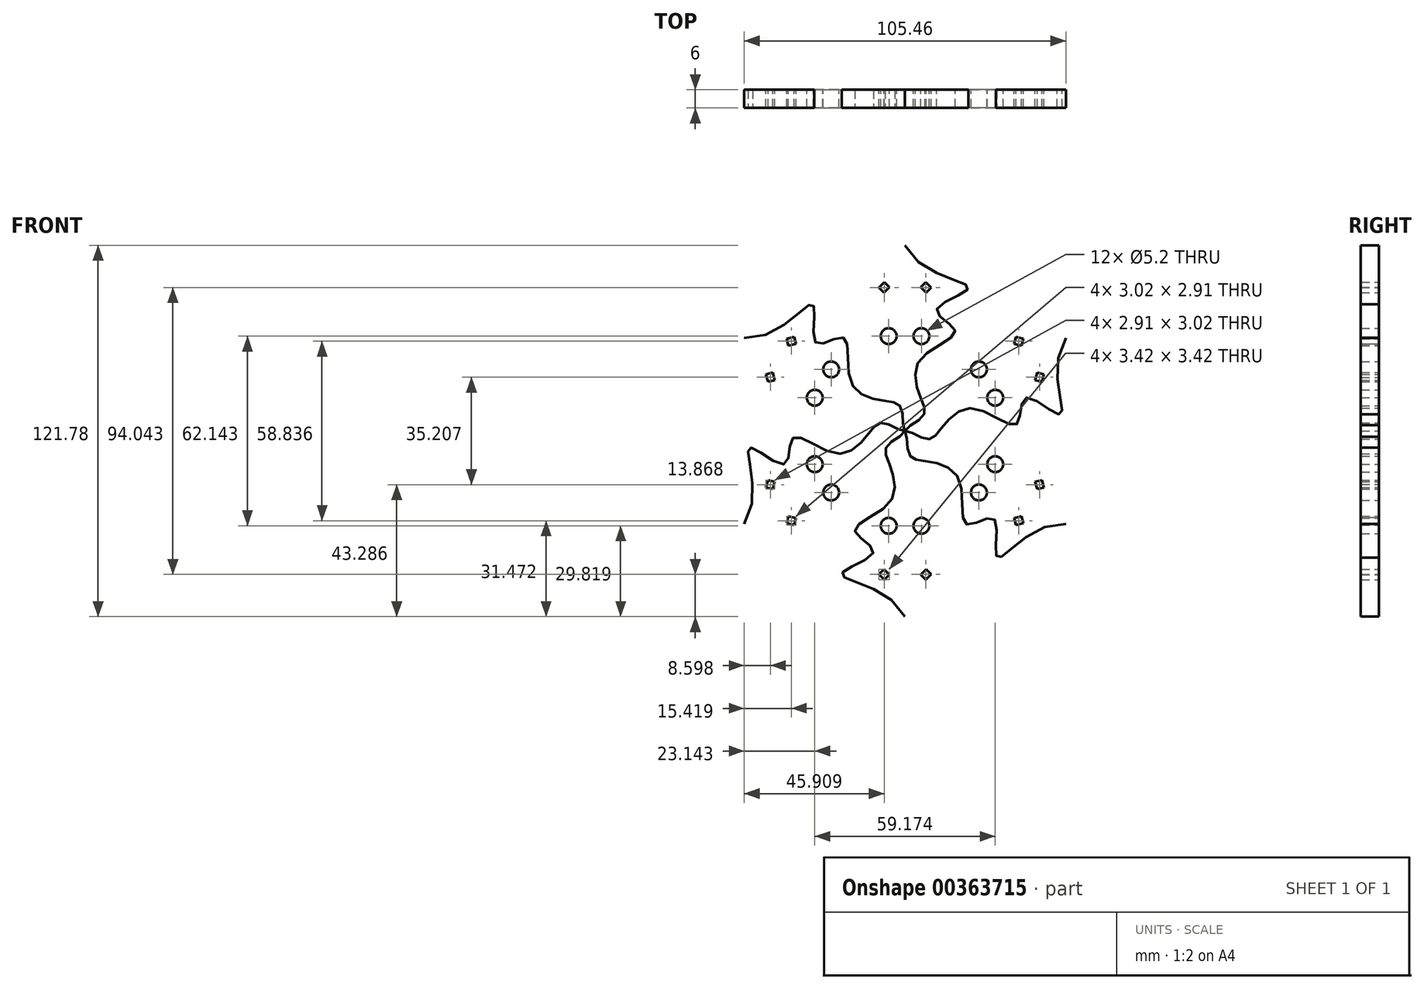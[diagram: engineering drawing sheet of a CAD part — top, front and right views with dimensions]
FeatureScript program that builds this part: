
annotation { "Feature Type Name" : "Feature", "Feature Type Description" : "" }
export const myFeature = defineFeature(function(context is Context, id is Id, definition is map)
    precondition{}
    {
        {
            var Q0;
            Q0=qCreatedBy(makeId("Front.planeOp"),FACE);
            var sketch = newSketch(context, id + "F0", { "sketchPlane" : qUnion([Q0])});
            skLineSegment(sketch, "E0", {"start": v(0, 0) * mm, "end": v(0, 65.18) * mm, "construction": true});
            skFitSpline(sketch, "E1", {"points": [v(0, 60.9) * mm, v(20.71, 46.79) * mm, v(10.36, 39.64) * mm, v(16.43, 32.86) * mm, v(4.83, 23.22) * mm, v(5.36, 10.36) * mm, v(5.9, 4.82) * mm, v(0, 0) * mm], "startDerivative": vector(73.99, -153.32) * mm, "endDerivative": vector(-12.46, -38.16) * mm});
            skCircle(sketch, "E2", {"center": v(5.36, 31.07) * mm, "radius": 2.6 * mm});
            skFitSpline(sketch, "E3.MirrorCS", {"points": [v(0, 60.9) * mm, v(-20.71, 46.79) * mm, v(-10.36, 39.64) * mm, v(-16.43, 32.86) * mm, v(-4.83, 23.22) * mm, v(-5.36, 10.36) * mm, v(-5.9, 4.82) * mm, v(0, 0) * mm], "startDerivative": vector(-73.99, -153.32) * mm, "endDerivative": vector(12.46, -38.16) * mm});
            skCircle(sketch, "E4.MirrorC", {"center": v(-5.36, 31.07) * mm, "radius": 2.6 * mm});
            skLineSegment(sketch, "E5.bottom", {"start": v(6.76, 48.73) * mm, "end": v(8.53, 46.96) * mm});
            skLineSegment(sketch, "E5.top", {"start": v(5.11, 47.08) * mm, "end": v(6.88, 45.31) * mm});
            skLineSegment(sketch, "E5.left", {"start": v(6.76, 48.73) * mm, "end": v(5.11, 47.08) * mm});
            skLineSegment(sketch, "E5.right", {"start": v(8.53, 46.96) * mm, "end": v(6.88, 45.31) * mm});
            skLineSegment(sketch, "E6.MirrorCS", {"start": v(-5.11, 47.08) * mm, "end": v(-6.88, 45.31) * mm});
            skLineSegment(sketch, "E7.MirrorCS", {"start": v(-6.76, 48.73) * mm, "end": v(-5.11, 47.08) * mm});
            skLineSegment(sketch, "E8.MirrorCS", {"start": v(-8.53, 46.96) * mm, "end": v(-6.88, 45.31) * mm});
            skLineSegment(sketch, "E9.MirrorCS", {"start": v(-6.76, 48.73) * mm, "end": v(-8.53, 46.96) * mm});
            skSolve(sketch);
        }
        {
            var Q0;
            Q0=makeQuery(id+"F0.imprint","IMPRINT",FACE,{"disambiguationData":[TD([[makeQuery(id+"F0.imprint","IMPRINT",EDGE,{"derivedFrom":sQuery(id+"F0.wireOp",EDGE,"E1")}),-1.0]])]});
            extrude(context, id + "F1", {"entities" : qUnion([Q0]), "depth" : 6 * mm});
        }
        {
            var Q0;
            Q0=qCreatedBy(makeId("Right.planeOp"),FACE);
            var sketch = newSketch(context, id + "F2", { "sketchPlane" : qUnion([Q0])});
            skLineSegment(sketch, "E10", {"start": v(0, 0) * mm, "end": v(-63.04, 0) * mm, "construction": true});
            skSolve(sketch);
        }
        {
            var Q0;
            Q0=makeQuery(id+"F1.opExtrude","SWEPT_BODY",BODY,{"disambiguationData":[OSD([sQuery(id+"F0.wireOp",EDGE,"E1"),sQuery(id+"F0.wireOp",EDGE,"E2"),sQuery(id+"F0.wireOp",EDGE,"E4.MirrorC"),sQuery(id+"F0.wireOp",EDGE,"E5.bottom"),sQuery(id+"F0.wireOp",EDGE,"E5.top"),sQuery(id+"F0.wireOp",EDGE,"E5.left"),sQuery(id+"F0.wireOp",EDGE,"E5.right"),sQuery(id+"F0.wireOp",EDGE,"E6.MirrorCS"),sQuery(id+"F0.wireOp",EDGE,"E7.MirrorCS"),sQuery(id+"F0.wireOp",EDGE,"E8.MirrorCS"),sQuery(id+"F0.wireOp",EDGE,"E9.MirrorCS"),sQuery(id+"F0.wireOp",EDGE,"E3.MirrorCS")])]});
            var Q1;
            Q1=sQuery(id+"F2.wireOp",EDGE,"E10");
            circularPattern(context, id + "F3", {"entities" : qUnion([Q0]), "axis" : qUnion([Q1]), "angle" : 360 * degree, "instanceCount" : 6, "equalSpace" : true});
        }
    });
